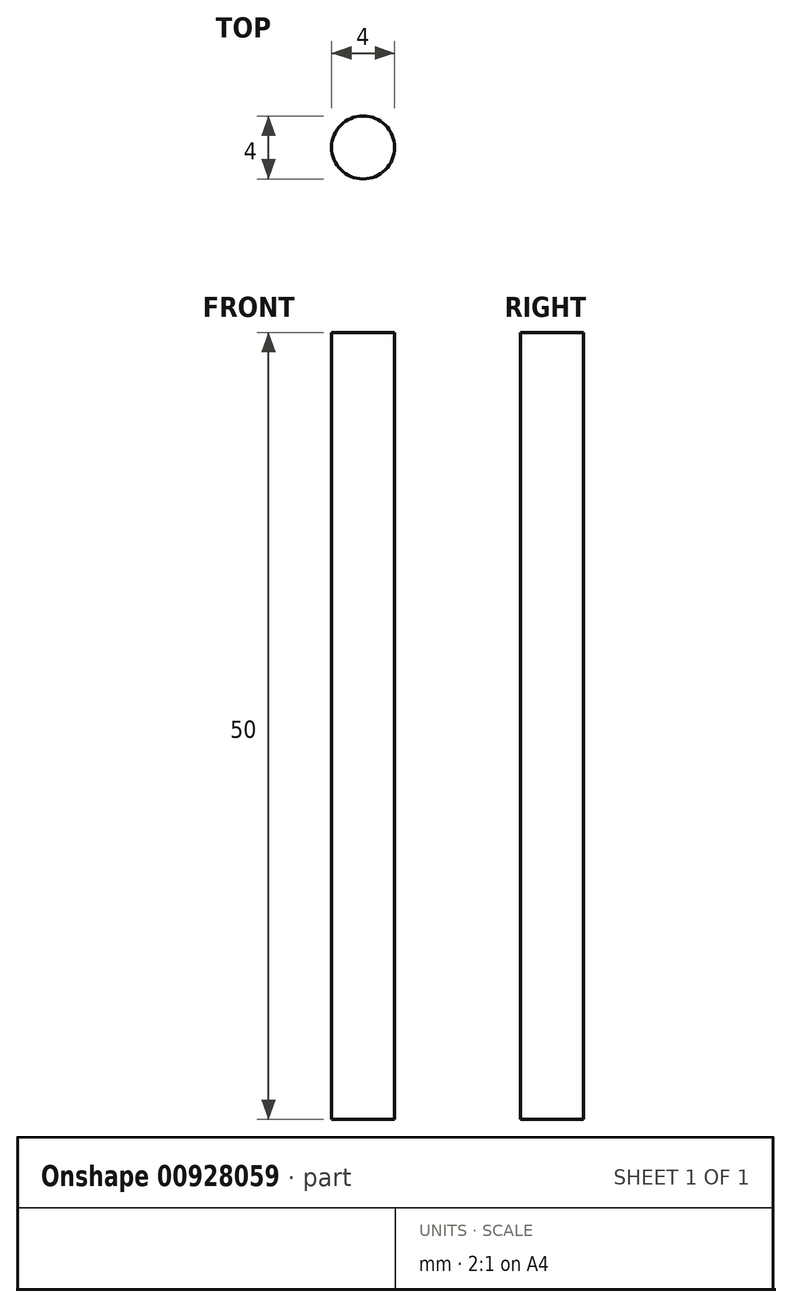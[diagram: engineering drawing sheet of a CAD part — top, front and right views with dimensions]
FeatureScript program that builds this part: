
annotation { "Feature Type Name" : "Feature", "Feature Type Description" : "" }
export const myFeature = defineFeature(function(context is Context, id is Id, definition is map)
    precondition{}
    {
        {
            var Q0;
            Q0=qCreatedBy(makeId("Top.planeOp"),FACE);
            var sketch = newSketch(context, id + "F0", { "sketchPlane" : qUnion([Q0])});
            skCircle(sketch, "E0", {"center": v(0, 0) * mm, "radius": 2 * mm});
            skSolve(sketch);
        }
        {
            var Q0;
            Q0 = qSketchRegion(id + "F0", true);
            extrude(context, id + "F1", {"entities" : qUnion([Q0]), "endBound" : BoundingType.SYMMETRIC, "depth" : 50 * mm, "offsetDistance" : 25 * mm});
        }
    });
